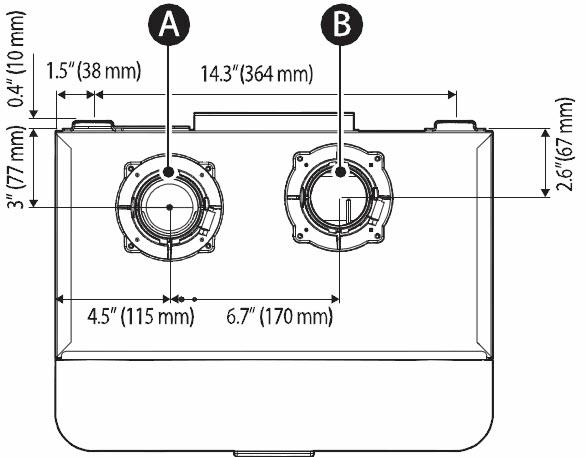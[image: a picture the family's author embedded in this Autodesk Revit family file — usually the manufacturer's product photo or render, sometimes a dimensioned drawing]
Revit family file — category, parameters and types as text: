
# Revit family: Water_Heater-Racks-Navien-NPE-11_Unit_Front---
name_source: partatom
category: Mechanical Equipment
revit_build: Autodesk Revit 2016 (Build: 20150220_1215(x64)
units: mm (PartAtom-declared; Revit-internal decimal feet)

## family parameters
Cut with Voids When Loaded = No
Host = Face
OmniClass Number = 23.65.35.11
OmniClass Title = Supply Water Heaters
Part Type = Normal
Room Calculation Point = No
Round Connector Dimension = Use Diameter
Shared = No

## types (4) — shared parameters
2" Exhaust/Intake = Yes
3" Exhaust/Intake = No
Apparent Load = 0 VA
Assembly Code = D3010500
Certifications = Energy Star | AHRI | CSA | CSA | NFS
Cold Water Inlet = 1"
Configuration = NPE_F11_4F3F_4F
Default Elevation = 48 "
Depth = 23.8 "
Description = 11 Unit Front
Exhaust = 2"
Finish = Metal - Navien - White
Flow Rate = 1 GPM
Flow Rate Note = 35°F (19°C) temp rise: 11.2 GPM (42 L/m) | 45°F (25°C) temp rise: 8.7 GPM (33 L/m) | 67°F (36°C) temp rise: NPE-240A: 5.6 GPM(21 L/m), NPE-240S: 5.7 GPM(22 L/m)
Frequency = 60 Hz
Gas Inlet = 1"
Heating Capacity = 120000.0 Btu/h
Heating Capacity Note = 19,900–199,900 (BTU/H)
Height = 65.5 "
Hot Water Outlet = 1"
Ignition = Electronic ignition
Installation Type = Indoor
Intake = 2"
Keynote = 22 33 00.A1
Manifold(s) = (1) 30019041A + (2) 30019043A
Manufacturer = Navien, Inc.
Manufacturer Fax Number = (949) 420-0430
Natural Gas Manifold Pressure = -0.05" WC to -0.58" WC
Natural Gas Supply Pressure = 3.5"–10.5" WC
Number of Poles = 1
Phase = 1
Power Factor = 1
Product Documentation Link = https://www.navieninc.com
Product Name = NPE Series Tankless Water Heaters w/ Racks
Product Page URL = https://www.navieninc.com
Propane Gas Manifold Pressure = -0.10" WC to -0.78" WC
Propane Gas Supply Pressure = 8"–13" WC
Rack(s) = (2) GFFM-KDIZUS-003 + (9) GFFM-KDIZUS-004
Required Cascade Operation Accessory = (11) 30014367A (Common Vent Damper & Cascade Communication Cable) or (10) GXXX000546 (Individual Vent Cascade Communication Cable)
Type Comments = For Wall Mount RL Manifold systems- Exclude Base & Add-on Racks
URL = https://www.navieninc.com
Venting = Exhaust: 2" PVC, CPVC, PP, SS / 2" special gas vent type BH (Class II, A/B/C) | Intake: 2" PVC, CPVC, PP, SS / 2" special gas vent type BH (Class II, A/B/C) | Vent clearances: 0" to combustibles
Venting Type = Forced draft direct vent
Version = 2016 - v1.0.a
Voltage = 120 V
Water Pressure = 15–150 PSI
Wi-Fi Ready = NaviLink Wi-Fi Control: PBCM-AS-001
Width = 242.3 "

## per-type parameters (varying)
| type | Constraints | Model | Natural Gas | Propane Gas | Recirculation Inlet | Recirculation Inlet Visibility | Tankless Water Heaters | Weight |
| Natural Gas - Recirculating System - NPE-240A(Advanced)-NG | 6 | (11) NPE-240A-NG | Yes | No | 0" | Yes | (11) NPE-240A-NG | 82.00 lbf |
| Natural Gas - NPE-240S(Standard)-NG | 7 | (11) NPE-240S-NG | Yes | No | 1" | No | (11) NPE-240S-NG | 75.00 lbf |
| Propane Gas - Recirculating System - NPE-240A(Advanced)-LPG | 6 | (11) NPE-240A-LPG | No | Yes | 0" | Yes | (11) NPE-240A-LPG | 82.00 lbf |
| Propane Gas - NPE-240S(Standard)-LPG | 7 | (11) NPE-240S-LPG | No | Yes | 1" | No | (11) NPE-240S-LPG | 75.00 lbf |

## geometry (parser evidence)
native form markers: Sweep x18
no freeform markers — native parametric forms only
